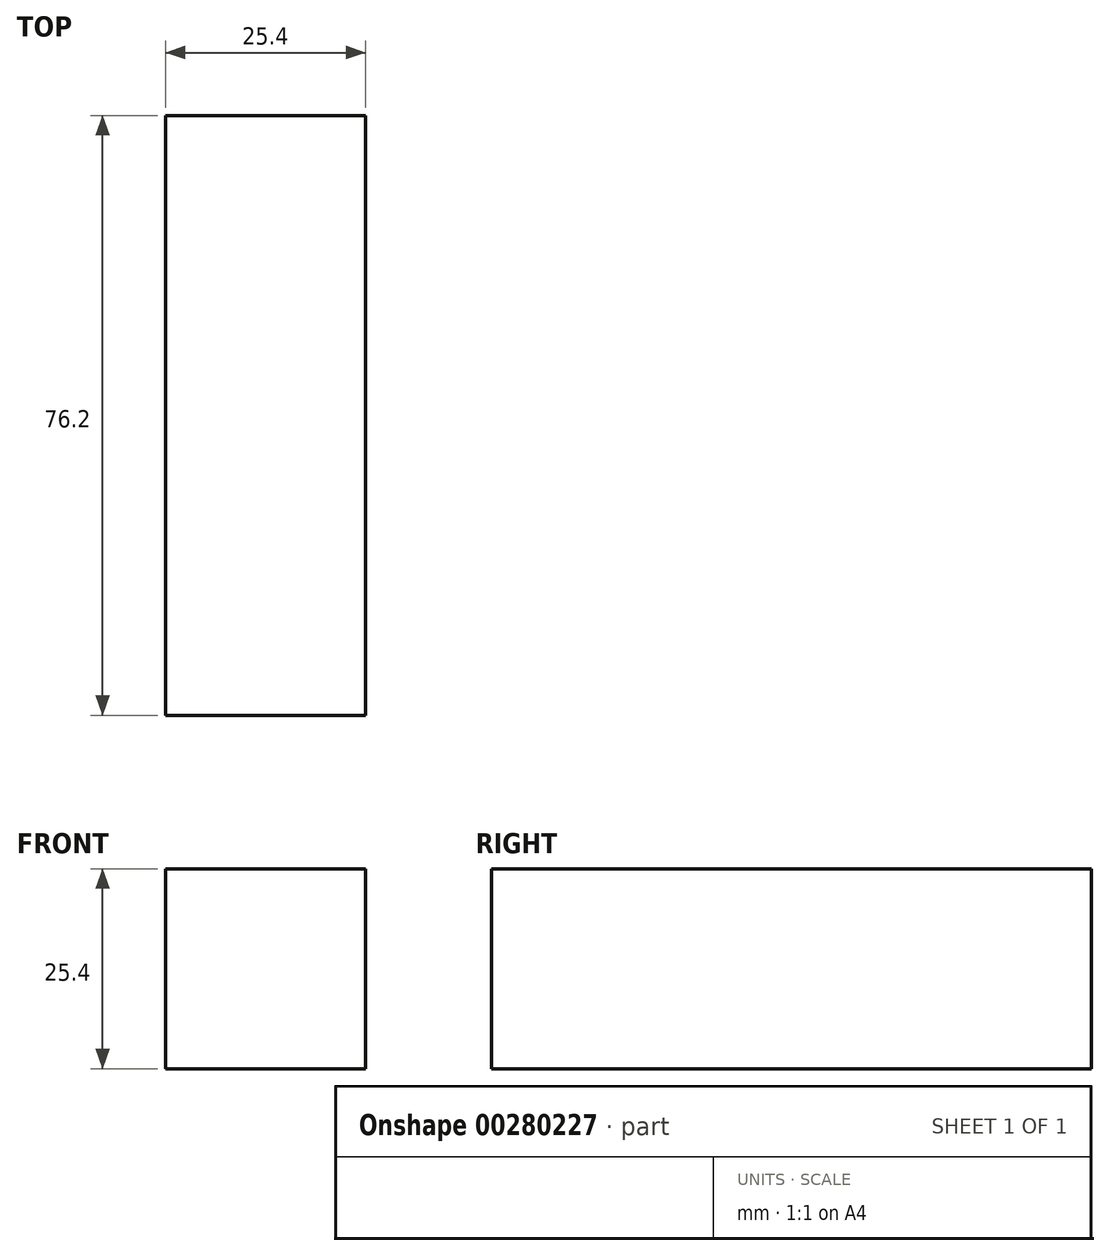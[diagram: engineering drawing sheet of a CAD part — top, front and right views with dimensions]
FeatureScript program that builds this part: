
annotation { "Feature Type Name" : "Feature", "Feature Type Description" : "" }
export const myFeature = defineFeature(function(context is Context, id is Id, definition is map)
    precondition{}
    {
        {
            var Q0;
            Q0=qCreatedBy(makeId("Front.planeOp"),FACE);
            var sketch = newSketch(context, id + "F0", { "sketchPlane" : qUnion([Q0])});
            skLineSegment(sketch, "E0.bottom", {"start": v(40.3, 46.42) * mm, "end": v(14.9, 46.42) * mm});
            skLineSegment(sketch, "E0.top", {"start": v(40.3, 21.02) * mm, "end": v(14.9, 21.02) * mm});
            skLineSegment(sketch, "E0.left", {"start": v(40.3, 46.42) * mm, "end": v(40.3, 21.02) * mm});
            skLineSegment(sketch, "E0.right", {"start": v(14.9, 46.42) * mm, "end": v(14.9, 21.02) * mm});
            skSolve(sketch);
        }
        {
            var Q0;
            Q0 = qSketchRegion(id + "F0", true);
            extrude(context, id + "F1", {"entities" : qUnion([Q0]), "depth" : 76.2 * mm});
        }
    });
